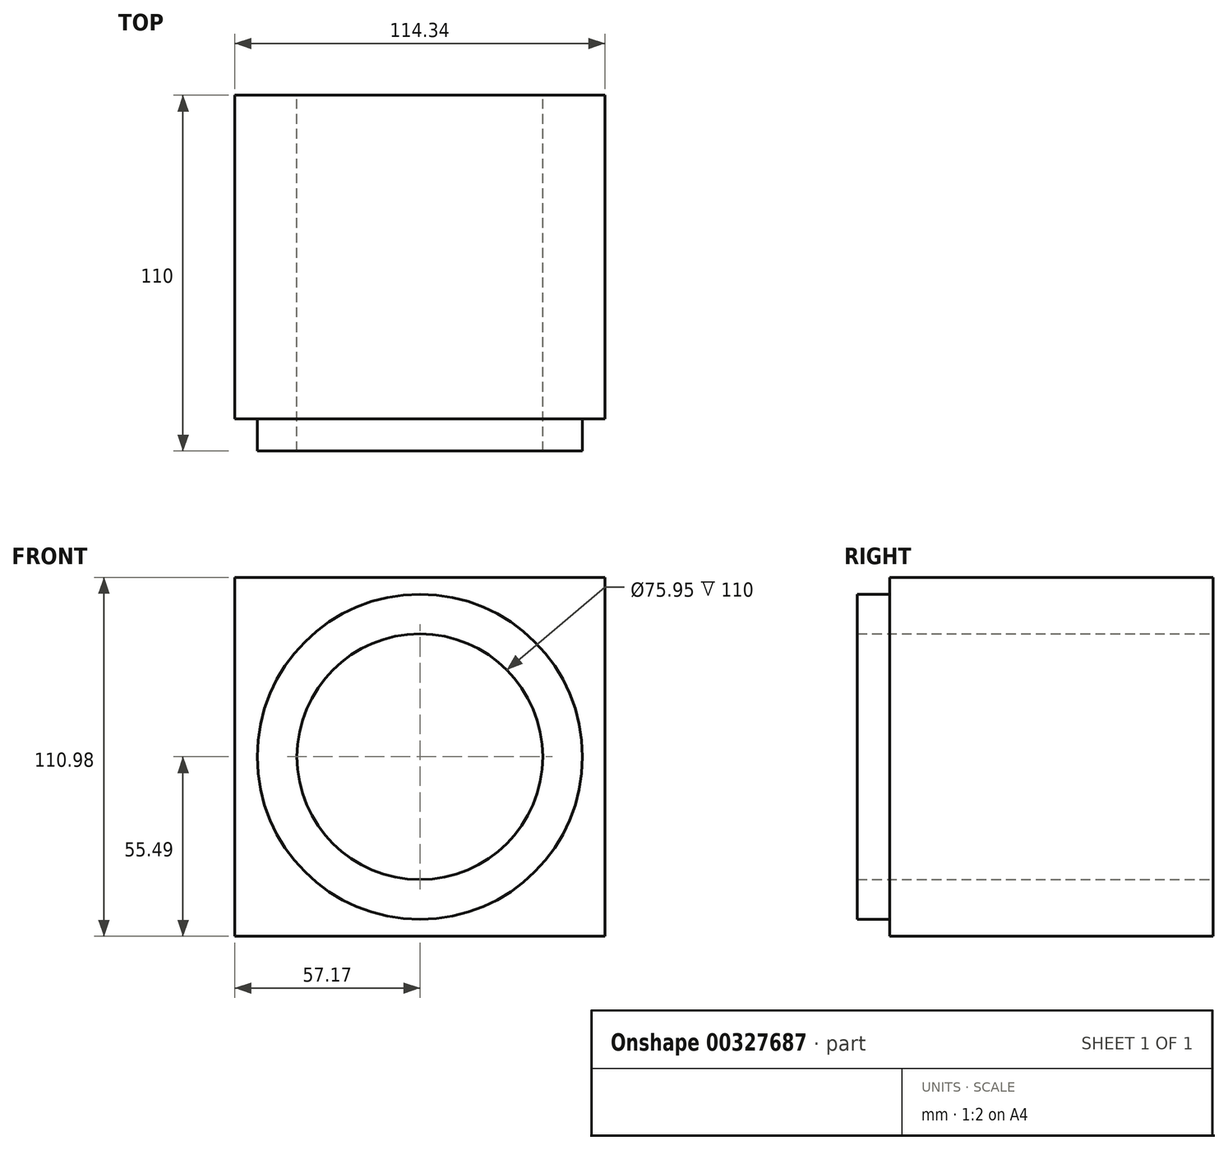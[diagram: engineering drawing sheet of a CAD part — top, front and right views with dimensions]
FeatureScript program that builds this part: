
annotation { "Feature Type Name" : "Feature", "Feature Type Description" : "" }
export const myFeature = defineFeature(function(context is Context, id is Id, definition is map)
    precondition{}
    {
        {
            var Q0;
            Q0=qCreatedBy(makeId("Front.planeOp"),FACE);
            var sketch = newSketch(context, id + "F0", { "sketchPlane" : qUnion([Q0])});
            skLineSegment(sketch, "E0.bottom", {"start": v(57.17, 55.49) * mm, "end": v(-57.17, 55.49) * mm});
            skLineSegment(sketch, "E0.top", {"start": v(57.17, -55.49) * mm, "end": v(-57.17, -55.49) * mm});
            skLineSegment(sketch, "E0.left", {"start": v(57.17, 55.49) * mm, "end": v(57.17, -55.49) * mm});
            skLineSegment(sketch, "E0.right", {"start": v(-57.17, 55.49) * mm, "end": v(-57.17, -55.49) * mm});
            skPoint(sketch, "E0.middle", {"position": v(0, 0) * mm});
            skCircle(sketch, "E1", {"center": v(0, 0) * mm, "radius": 37.98 * mm});
            skCircle(sketch, "E2", {"center": v(0, 0) * mm, "radius": 26.02 * mm});
            skSolve(sketch);
        }
        {
            var Q0;
            Q0=makeQuery(id+"F0.imprint","IMPRINT",FACE,{"disambiguationData":[TD([[makeQuery(id+"F0.imprint","IMPRINT",EDGE,{"derivedFrom":sQuery(id+"F0.wireOp",EDGE,"E0.bottom")}),1.0]])]});
            extrude(context, id + "F1", {"entities" : qUnion([Q0]), "depth" : 100 * mm});
        }
        {
            var Q0;
            Q0=makeQuery(id+"F1.opExtrude","CAP_FACE",FACE,{"disambiguationData":[OSD([sQuery(id+"F0.wireOp",EDGE,"E0.bottom"),sQuery(id+"F0.wireOp",EDGE,"E0.top"),sQuery(id+"F0.wireOp",EDGE,"E0.left"),sQuery(id+"F0.wireOp",EDGE,"E0.right"),sQuery(id+"F0.wireOp",EDGE,"E1")])],"isStart":false});
            var sketch = newSketch(context, id + "F2", { "sketchPlane" : qUnion([Q0])});
            skCircle(sketch, "E3", {"center": v(0, 0) * mm, "radius": 50.27 * mm});
            skCircle(sketch, "E4.0", {"center": v(0, 0) * mm, "radius": 37.98 * mm});
            skSolve(sketch);
        }
        {
            var Q0;
            Q0 = qSketchRegion(id + "F2", true);
            extrude(context, id + "F3", {"entities" : qUnion([Q0]), "operationType" : NewBodyOperationType.ADD, "depth" : 10 * mm});
        }
    });
